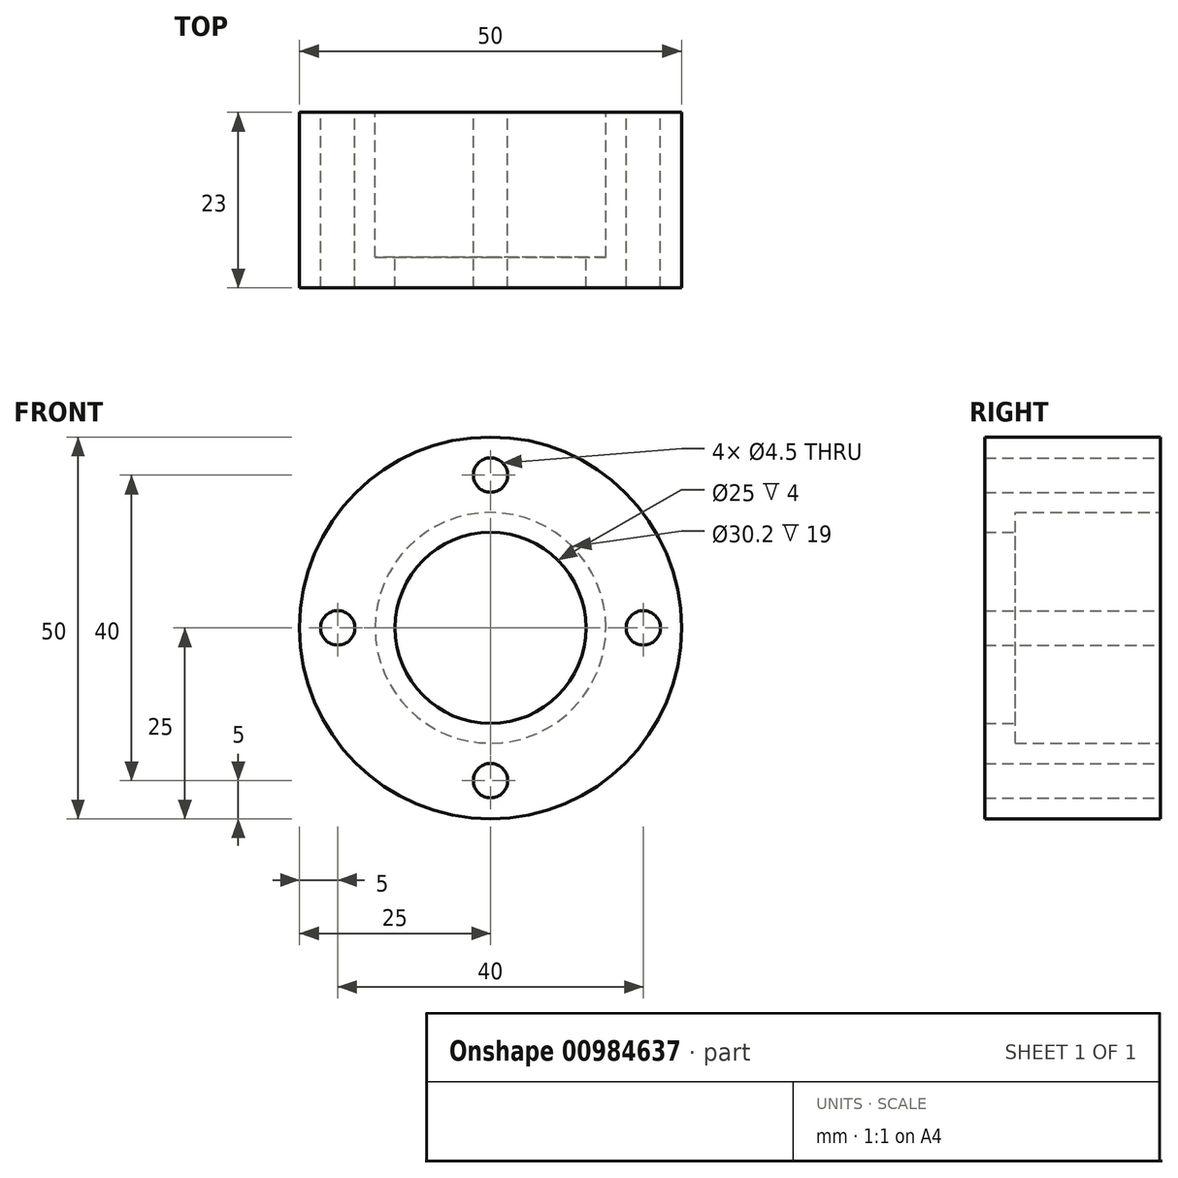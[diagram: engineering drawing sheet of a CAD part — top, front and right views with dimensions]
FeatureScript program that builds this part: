
annotation { "Feature Type Name" : "Feature", "Feature Type Description" : "" }
export const myFeature = defineFeature(function(context is Context, id is Id, definition is map)
    precondition{}
    {
        {
            var Q0;
            Q0=qCreatedBy(makeId("Front.planeOp"),FACE);
            var sketch = newSketch(context, id + "F0", { "sketchPlane" : qUnion([Q0])});
            skCircle(sketch, "E0", {"center": v(0, 0) * mm, "radius": 25 * mm});
            skCircle(sketch, "E1", {"center": v(0, 0) * mm, "radius": 12.5 * mm});
            skSolve(sketch);
        }
        {
            var Q0;
            Q0 = qSketchRegion(id + "F0", true);
            extrude(context, id + "F1", {"entities" : qUnion([Q0]), "depth" : 23 * mm, "offsetDistance" : 25 * mm});
        }
        {
            var Q0;
            Q0=qCreatedBy(makeId("Front.planeOp"),FACE);
            var sketch = newSketch(context, id + "F2", { "sketchPlane" : qUnion([Q0])});
            skCircle(sketch, "E2", {"center": v(0, 0) * mm, "radius": 15.1 * mm});
            skSolve(sketch);
        }
        {
            var Q0;
            Q0 = qSketchRegion(id + "F2", true);
            extrude(context, id + "F3", {"entities" : qUnion([Q0]), "operationType" : NewBodyOperationType.REMOVE, "depth" : 19 * mm, "offsetDistance" : 25 * mm});
        }
        {
            var Q0;
            Q0=makeQuery(id+"F1.opExtrude","CAP_FACE",FACE,{"disambiguationData":[OSD([sQuery(id+"F0.wireOp",EDGE,"E0"),sQuery(id+"F0.wireOp",EDGE,"E1")])],"isStart":true});
            var sketch = newSketch(context, id + "F4", { "sketchPlane" : qUnion([Q0])});
            skCircle(sketch, "E3", {"center": v(0, 0) * mm, "radius": 20 * mm, "construction": true});
            skCircle(sketch, "E4", {"center": v(20, 0) * mm, "radius": 2.25 * mm});
            skCircle(sketch, "E5", {"center": v(0, -20) * mm, "radius": 2.25 * mm});
            skCircle(sketch, "E6", {"center": v(-20, 0) * mm, "radius": 2.25 * mm});
            skCircle(sketch, "E7", {"center": v(0, 20) * mm, "radius": 2.25 * mm});
            skSolve(sketch);
        }
        {
            var Q0;
            Q0 = qSketchRegion(id + "F4", true);
            extrude(context, id + "F5", {"entities" : qUnion([Q0]), "operationType" : NewBodyOperationType.REMOVE, "oppositeDirection" : true, "depth" : 25 * mm, "offsetDistance" : 25 * mm});
        }
    });
